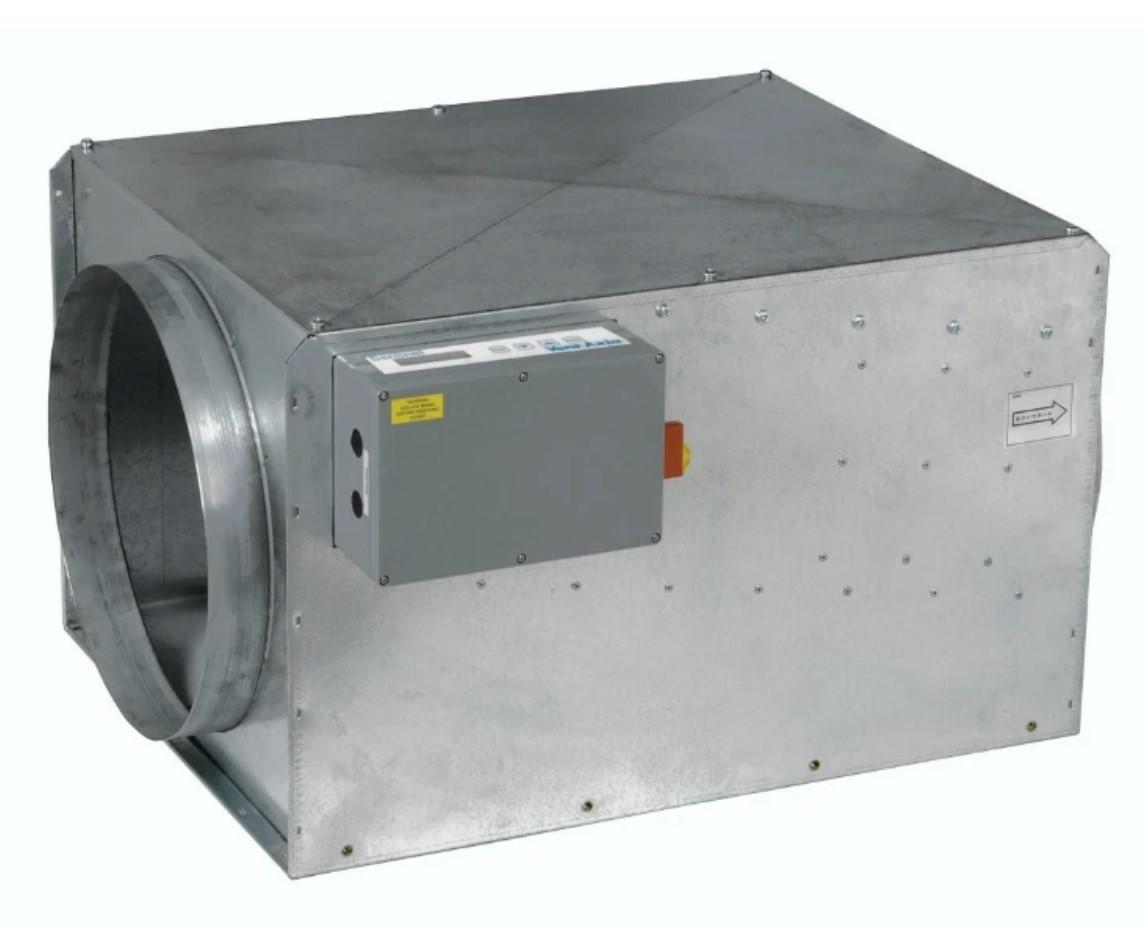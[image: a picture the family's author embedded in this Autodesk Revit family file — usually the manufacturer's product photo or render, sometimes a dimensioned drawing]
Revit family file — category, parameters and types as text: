
# Revit family: CADS_Vent-Axia_MechEquip_Fan_SENT_DBoxTwin - EXTRACT
name_source: partatom
category: Mechanical Equipment
units: mm (PartAtom-declared; Revit-internal decimal feet)

## family parameters
Classification = None
Cut with Voids When Loaded = No
Host = Face
OmniClass Number = 23.75.35.17.11
OmniClass Title = Fans for Air Ductwork
Part Type = Normal
Room Calculation Point = No
Round Connector Dimension = Use Diameter
Shared = No

## types (13) — shared parameters
AirflowRateRange = 0.0 L/s
AssemblyPlace = UNKNOWN
AssetType = FIXED
Default Elevation = 1219 mm
DurationUnit = Year
EBHoffset = 206 mm
EBVoffset = 80 mm
ExteriorInsulation = No
Fitting Type = Ignore
GrossWeight = 0.00 kg
HasProtectiveEarth = No
IsExtendedWarranty = No
ManufacturerAddress = Fleming Way
Crawley 
RH10 9YX
Quantity = 1
RatedCurrent = 0 A
RatedVoltage = 0 V
SpigotCLHeight = 62 mm
Status = New
Type Image = <None>
WarrantyGuarantor = Vent-Axia Limited
WorkingPressure = 0.0 Pa
zero-valued in all types: CADS_Index, CADS_Usage, ExpectedServiceLife, H, NumberOfPoles, OutOffset, W

## per-type parameters (varying)
| type | L | ModelReference | NominalDiameter | NominalHeight | NominalLength | NominalWidth |
| SENT100T | 610 mm  [stored 2.00131 ft] | SENTINEL 100T HEIRARCHY | 100 mm  [stored 0.328084 ft] | 256 mm  [stored 0.839895 ft] | 610 mm  [stored 2.00131 ft] | 591 mm  [stored 1.93898 ft] |
| SENT125T | 610 mm  [stored 2.00131 ft] | SENTINEL 125T HEIRARCHY | 125 mm  [stored 0.410105 ft] | 256 mm  [stored 0.839895 ft] | 610 mm  [stored 2.00131 ft] | 591 mm  [stored 1.93898 ft] |
| SENT125T/CP | 610 mm  [stored 2.00131 ft] | SENTINEL 125 TWIN CP | 125 mm  [stored 0.410105 ft] | 256 mm  [stored 0.839895 ft] | 610 mm  [stored 2.00131 ft] | 591 mm  [stored 1.93898 ft] |
| SENT150T | 610 mm  [stored 2.00131 ft] | SENTINEL 150 TWIN | 150 mm | 256 mm  [stored 0.839895 ft] | 610 mm  [stored 2.00131 ft] | 591 mm  [stored 1.93898 ft] |
| SENT200T | 801 mm | SENTINEL 200T HIERARCHY | 200 mm  [stored 0.656168 ft] | 343 mm | 801 mm | 703 mm |
| SENT250S/CP | 925 mm | SENTINEL 250 CONST.PRESS | 250 mm  [stored 0.82021 ft] | 354 mm | 925 mm | 798 mm |
| SENT250T | 925 mm | SENTINEL 250T HIERARCHY | 250 mm  [stored 0.82021 ft] | 354 mm | 925 mm | 798 mm |
| SENT250T/CP | 925 mm | SENTINEL 250 TWIN CP | 315 mm | 354 mm | 925 mm | 798 mm |
| SENT315T | 1255 mm | SENTINEL 315T HIERARCHY | 315 mm | 536 mm | 1255 mm | 1145 mm |
| SENT315T/CP | 1255 mm | SENTINEL 315 TWIN CP | 315 mm | 536 mm | 1255 mm | 1145 mm |
| SENT400T | 1255 mm | SENTINEL 400T HIERARCHY | 400 mm | 536 mm | 1255 mm | 1145 mm |
| SENT400T/CP | 1255 mm | SENTINEL 400 TWIN CP | 400 mm | 536 mm | 1255 mm | 1145 mm |
| SENT500T | 1492 mm | SENTINEL 500T HIERARCHY | 500 mm | 675 mm | 1492 mm | 1533 mm |

note: column(s) folded — value = type name in every type: ModelNumber

note: [stored X ft] marks values corroborated as IEEE doubles in the binary element streams (Revit-internal decimal feet)

## geometry (parser evidence)
native form markers: Sweep x3
no freeform markers — native parametric forms only
